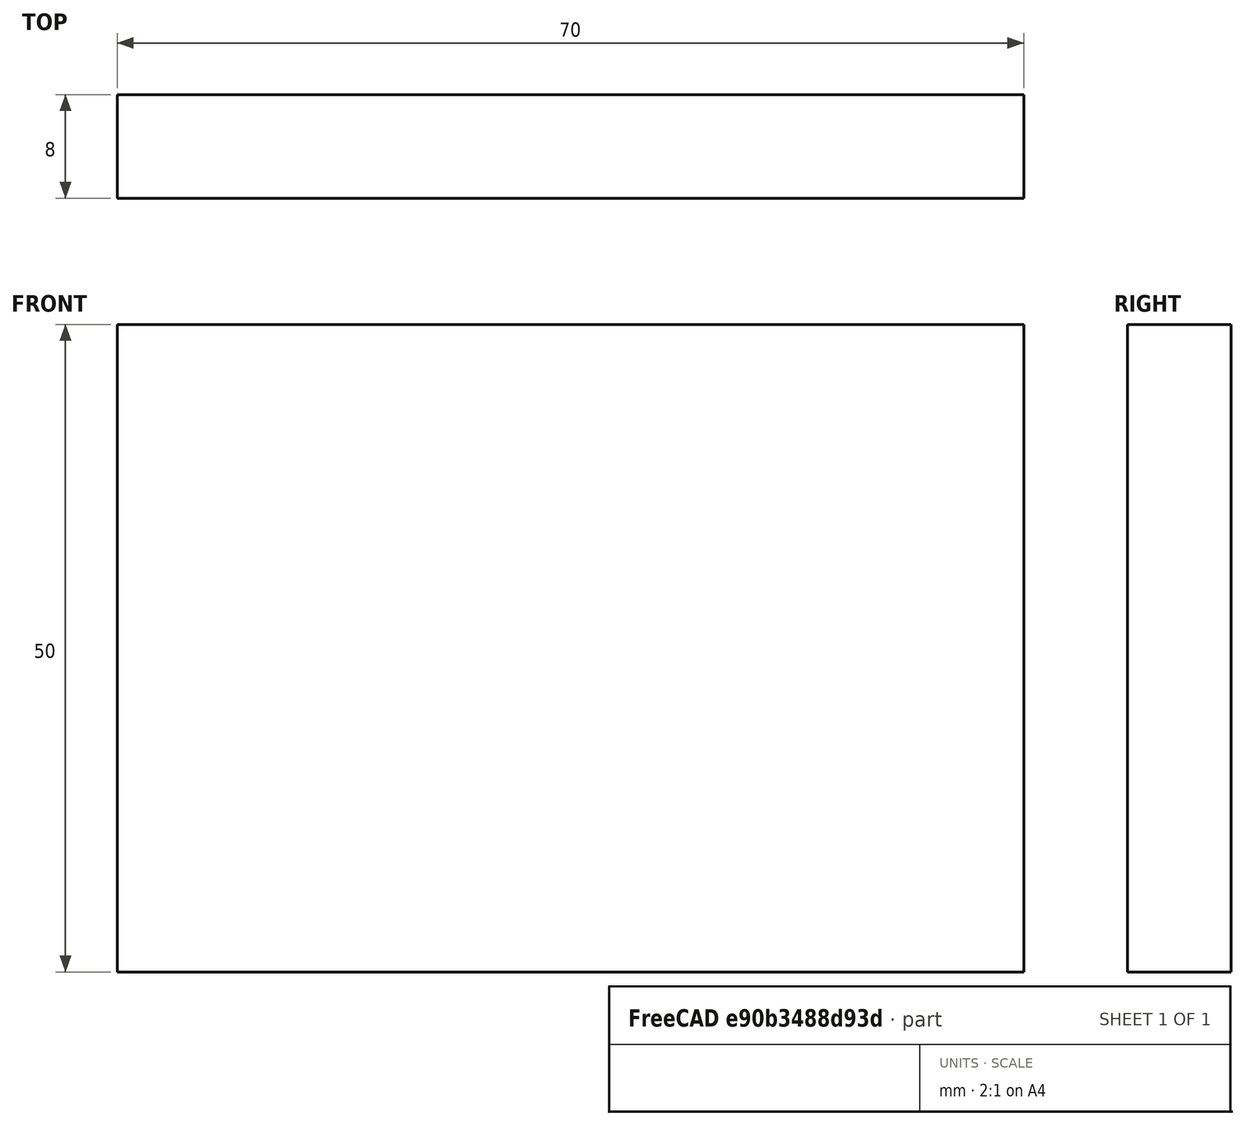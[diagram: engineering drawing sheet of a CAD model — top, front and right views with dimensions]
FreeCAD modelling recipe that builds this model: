
FCSTD DOCUMENT  (FreeCAD 0.15R4671 (Git))
Label: Flat Bar 70x8 EN10058 S235JR
License: All rights reserved
LicenseURL: http://en.wikipedia.org/wiki/All_rights_reserved
objects: Sketcher::SketchObject×1, Part::Extrusion×1
note: 2 computed .brp shape members not serialized (recipe doc carries the construction recipe); baked Part::Feature solids carry a one-line shape summary decoded from their .brp

FEATURE [Sketcher::SketchObject] Sketch
  sketch-geometry (4):
    g0: LineSegment StartX=-35 StartY=-4 StartZ=0 EndX=35 EndY=-4 EndZ=0
    g1: LineSegment StartX=35 StartY=-4 StartZ=0 EndX=35 EndY=4 EndZ=0
    g2: LineSegment StartX=35 StartY=4 StartZ=0 EndX=-35 EndY=4 EndZ=0
    g3: LineSegment StartX=-35 StartY=4 StartZ=0 EndX=-35 EndY=-4 EndZ=0
  constraints (12):
    c: Coincident(g0,g1)
    c: Coincident(g1,g2)
    c: Coincident(g2,g3)
    c: Coincident(g3,g0)
    c: Horizontal(g0)
    c: Horizontal(g2)
    c: Vertical(g1)
    c: Vertical(g3)
    c: Symmetric(g1,g2,g-2)
    c: Symmetric(g0,g1,g-1)
    c: DistanceY(g1) = 8
    c: DistanceX(g0) = 70
FEATURE [Part::Extrusion] Extrude  label="Flat Bar 70x8 EN10058 S235JR"
  Base = -> Sketch
  Dir = (0,0,50)
  Solid = true
